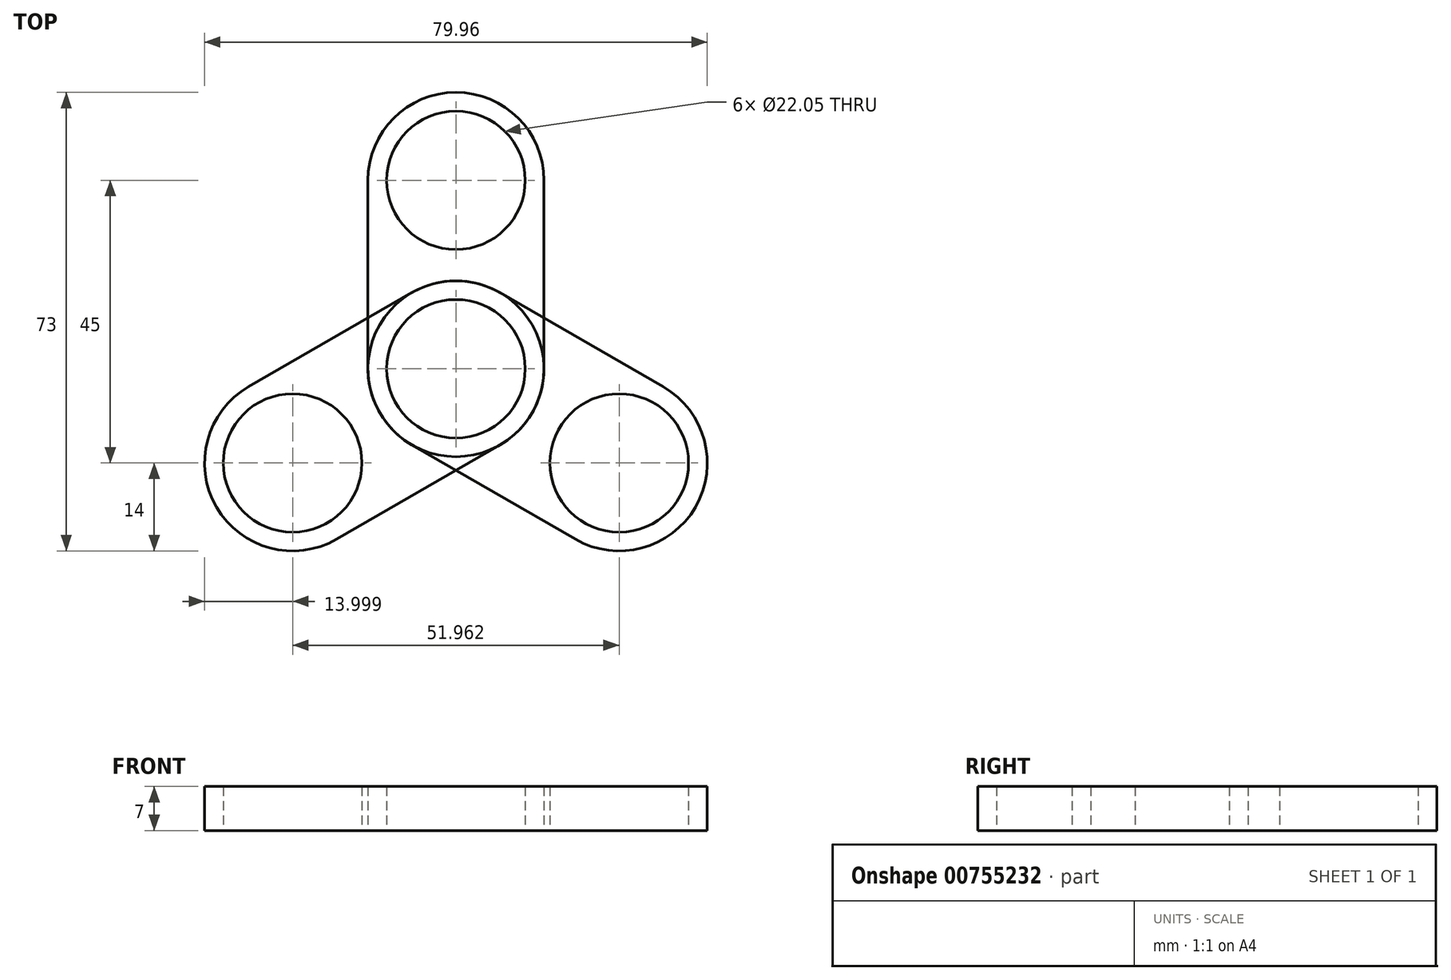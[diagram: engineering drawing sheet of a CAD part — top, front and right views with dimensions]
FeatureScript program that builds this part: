
annotation { "Feature Type Name" : "Feature", "Feature Type Description" : "" }
export const myFeature = defineFeature(function(context is Context, id is Id, definition is map)
    precondition{}
    {
        {
            var Q0;
            Q0=qCreatedBy(makeId("Top.planeOp"),FACE);
            var sketch = newSketch(context, id + "F0", { "sketchPlane" : qUnion([Q0])});
            skLineSegment(sketch, "E0.bottom", {"start": v(0, 0) * mm, "end": v(28, 0) * mm});
            skLineSegment(sketch, "E0.top", {"start": v(0, 30) * mm, "end": v(28, 30) * mm});
            skLineSegment(sketch, "E0.left", {"start": v(0, 0) * mm, "end": v(0, 30) * mm});
            skLineSegment(sketch, "E0.right", {"start": v(28, 0) * mm, "end": v(28, 30) * mm});
            skCircle(sketch, "E1", {"center": v(14, 30) * mm, "radius": 14 * mm});
            skCircle(sketch, "E2", {"center": v(14, 0) * mm, "radius": 14 * mm});
            skCircle(sketch, "E3", {"center": v(14, 30) * mm, "radius": 11.03 * mm});
            skCircle(sketch, "E4", {"center": v(14, 0) * mm, "radius": 11.03 * mm});
            skSolve(sketch);
        }
        {
            var Q0;
            {var subQ1=sQuery(id+"F0.wireOp",EDGE,"E0.top");var subQ3=sQuery(id+"F0.wireOp",EDGE,"E3");var subQ4=makeQuery(id+"F0.imprint","INTERSECT",VERTEX,{"disambiguationData":[OD(0.0)],"derivedFrom":[subQ1,subQ3]});Q0=makeQuery(id+"F0.imprint","IMPRINT",FACE,{"disambiguationData":[TD([[makeQuery(id+"F0.imprint","IMPRINT",EDGE,{"disambiguationData":[TD([[subQ4,1.0]])],"derivedFrom":subQ3}),-1.0]])]});}
            var Q1;
            {var subQ1=sQuery(id+"F0.wireOp",EDGE,"E0.top");var subQ3=sQuery(id+"F0.wireOp",EDGE,"E3");var subQ4=makeQuery(id+"F0.imprint","INTERSECT",VERTEX,{"disambiguationData":[OD(0.0)],"derivedFrom":[subQ1,subQ3]});Q1=makeQuery(id+"F0.imprint","IMPRINT",FACE,{"disambiguationData":[TD([[makeQuery(id+"F0.imprint","IMPRINT",EDGE,{"disambiguationData":[TD([[subQ4,-1.0]])],"derivedFrom":subQ3}),-1.0]])]});}
            var Q2;
            {var subQ0=sQuery(id+"F0.wireOp",EDGE,"E0.left");Q2=makeQuery(id+"F0.imprint","IMPRINT",FACE,{"disambiguationData":[TD([[makeQuery(id+"F0.imprint","IMPRINT",EDGE,{"derivedFrom":subQ0}),-1.0]])]});}
            var Q3;
            {var subQ1=sQuery(id+"F0.wireOp",EDGE,"E0.bottom");var subQ3=sQuery(id+"F0.wireOp",EDGE,"E4");var subQ4=makeQuery(id+"F0.imprint","INTERSECT",VERTEX,{"disambiguationData":[OD(0.0)],"derivedFrom":[subQ1,subQ3]});Q3=makeQuery(id+"F0.imprint","IMPRINT",FACE,{"disambiguationData":[TD([[makeQuery(id+"F0.imprint","IMPRINT",EDGE,{"disambiguationData":[TD([[subQ4,1.0]])],"derivedFrom":subQ3}),-1.0]])]});}
            var Q4;
            {var subQ1=sQuery(id+"F0.wireOp",EDGE,"E0.bottom");var subQ3=sQuery(id+"F0.wireOp",EDGE,"E4");var subQ4=makeQuery(id+"F0.imprint","INTERSECT",VERTEX,{"disambiguationData":[OD(0.0)],"derivedFrom":[subQ1,subQ3]});Q4=makeQuery(id+"F0.imprint","IMPRINT",FACE,{"disambiguationData":[TD([[makeQuery(id+"F0.imprint","IMPRINT",EDGE,{"disambiguationData":[TD([[subQ4,-1.0]])],"derivedFrom":subQ3}),-1.0]])]});}
            extrude(context, id + "F1", {"entities" : qUnion([Q0, Q1, Q2, Q3, Q4]), "depth" : 7 * mm, "offsetDistance" : 25 * mm});
        }
        {
            var Q0;
            Q0=makeQuery(id+"F1.opExtrude","SWEPT_BODY",BODY,{"disambiguationData":[OSD([sQuery(id+"F0.wireOp",EDGE,"E0.left"),sQuery(id+"F0.wireOp",EDGE,"E0.right"),sQuery(id+"F0.wireOp",EDGE,"E1"),sQuery(id+"F0.wireOp",EDGE,"E2"),sQuery(id+"F0.wireOp",EDGE,"E3"),sQuery(id+"F0.wireOp",EDGE,"E4")])]});
            var Q1;
            Q1=makeQuery(id+"F1.opExtrude","SWEPT_FACE",FACE,{"disambiguationData":[OSD([sQuery(id+"F0.wireOp",EDGE,"E2")])]});
            circularPattern(context, id + "F2", {"entities" : qUnion([Q0]), "axis" : qUnion([Q1]), "angle" : 360 * degree, "instanceCount" : 3, "equalSpace" : true});
        }
    });
